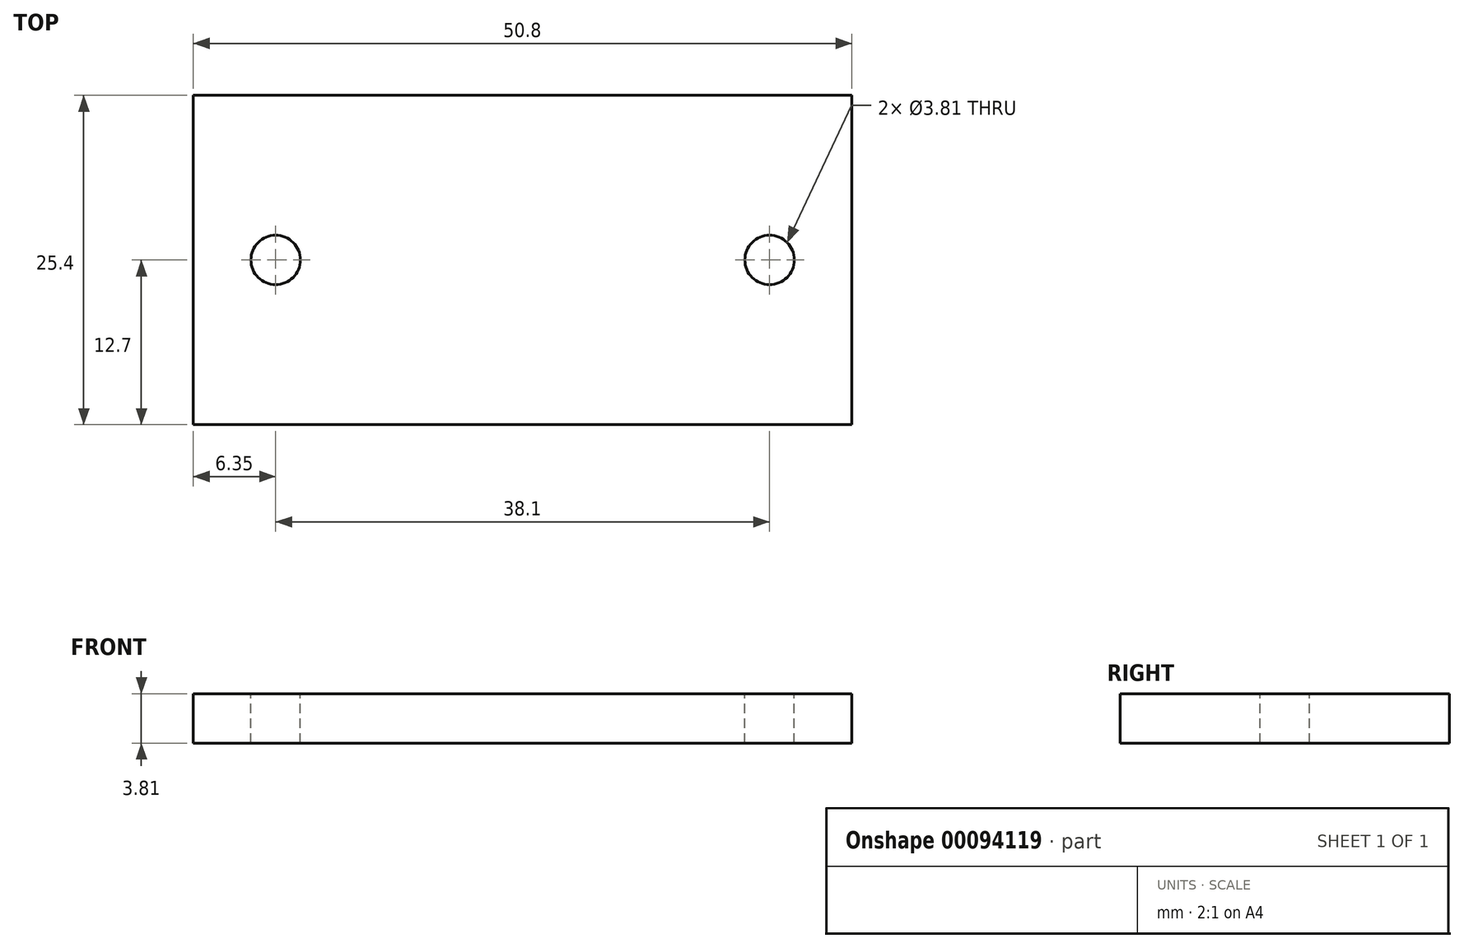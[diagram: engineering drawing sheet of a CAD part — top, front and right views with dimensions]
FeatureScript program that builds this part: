
annotation { "Feature Type Name" : "Feature", "Feature Type Description" : "" }
export const myFeature = defineFeature(function(context is Context, id is Id, definition is map)
    precondition{}
    {
        {
            var Q0;
            Q0=qCreatedBy(makeId("Front.planeOp"),FACE);
            var sketch = newSketch(context, id + "F0", { "sketchPlane" : qUnion([Q0])});
            skLineSegment(sketch, "E0.bottom", {"start": v(-25.4, 0) * mm, "end": v(25.4, 0) * mm});
            skLineSegment(sketch, "E0.top", {"start": v(-25.4, 3.81) * mm, "end": v(25.4, 3.8) * mm});
            skLineSegment(sketch, "E0.left", {"start": v(-25.4, 0) * mm, "end": v(-25.4, 3.81) * mm});
            skLineSegment(sketch, "E0.right", {"start": v(25.4, 0) * mm, "end": v(25.4, 3.81) * mm});
            skLineSegment(sketch, "E1.bottom", {"start": v(-12.7, 3.81) * mm, "end": v(12.7, 3.8) * mm});
            skLineSegment(sketch, "E1.top", {"start": v(-12.7, 29.21) * mm, "end": v(12.7, 29.21) * mm});
            skLineSegment(sketch, "E1.left", {"start": v(-12.7, 3.8) * mm, "end": v(-12.7, 29.21) * mm});
            skLineSegment(sketch, "E1.right", {"start": v(12.7, 3.8) * mm, "end": v(12.7, 29.21) * mm});
            skPoint(sketch, "E2", {"position": v(0, 3.8) * mm});
            skSolve(sketch);
        }
        {
            var Q0;
            Q0=makeQuery(id+"F0.imprint","IMPRINT",FACE,{"disambiguationData":[TD([[makeQuery(id+"F0.imprint","IMPRINT",EDGE,{"derivedFrom":sQuery(id+"F0.wireOp",EDGE,"E1.bottom")}),1.0]])]});
            var Q1;
            Q1=makeQuery(id+"F0.imprint","IMPRINT",FACE,{"disambiguationData":[TD([[makeQuery(id+"F0.imprint","IMPRINT",EDGE,{"derivedFrom":sQuery(id+"F0.wireOp",EDGE,"E0.bottom")}),1.0]])]});
            extrude(context, id + "F1", {"entities" : qUnion([Q0, Q1]), "depth" : 25.4 * mm});
        }
        {
            var Q0;
            Q0=makeQuery(id+"F1.opExtrude","CAP_FACE",FACE,{"disambiguationData":[OSD([sQuery(id+"F0.wireOp",EDGE,"E0.bottom"),sQuery(id+"F0.wireOp",EDGE,"E0.top"),sQuery(id+"F0.wireOp",EDGE,"E0.left"),sQuery(id+"F0.wireOp",EDGE,"E0.right"),sQuery(id+"F0.wireOp",EDGE,"E1.top"),sQuery(id+"F0.wireOp",EDGE,"E1.left"),sQuery(id+"F0.wireOp",EDGE,"E1.right")])],"isStart":true});
            var sketch = newSketch(context, id + "F2", { "sketchPlane" : qUnion([Q0])});
            skCircle(sketch, "E3", {"center": v(0, 16.51) * mm, "radius": 4 * mm});
            skSolve(sketch);
        }
        {
            var Q0;
            Q0=makeQuery(id+"F2.imprint","IMPRINT",FACE,{"disambiguationData":[TD([[makeQuery(id+"F2.imprint","IMPRINT",EDGE,{"derivedFrom":sQuery(id+"F2.wireOp",EDGE,"E3")}),1.0]])]});
            extrude(context, id + "F3", {"entities" : qUnion([Q0]), "operationType" : NewBodyOperationType.REMOVE, "endBound" : BoundingType.THROUGH_ALL, "oppositeDirection" : true, "depth" : 25.4 * mm});
        }
        {
            var Q0;
            Q0=makeQuery(id+"F1.opExtrude","CAP_FACE",FACE,{"disambiguationData":[OSD([sQuery(id+"F0.wireOp",EDGE,"E0.bottom"),sQuery(id+"F0.wireOp",EDGE,"E0.top"),sQuery(id+"F0.wireOp",EDGE,"E0.left"),sQuery(id+"F0.wireOp",EDGE,"E0.right"),sQuery(id+"F0.wireOp",EDGE,"E1.top"),sQuery(id+"F0.wireOp",EDGE,"E1.left"),sQuery(id+"F0.wireOp",EDGE,"E1.right")])],"isStart":true});
            var sketch = newSketch(context, id + "F4", { "sketchPlane" : qUnion([Q0])});
            skCircle(sketch, "E4.0", {"center": v(0, 16.51) * mm, "radius": 4 * mm});
            skCircle(sketch, "E5.cCircle", {"center": v(0, 16.51) * mm, "radius": 6.35 * mm, "construction": true});
            skLineSegment(sketch, "E5.0", {"start": v(3.67, 22.86) * mm, "end": v(7.33, 16.51) * mm});
            skLineSegment(sketch, "E5.1", {"start": v(7.33, 16.51) * mm, "end": v(3.67, 10.16) * mm});
            skLineSegment(sketch, "E5.2", {"start": v(3.67, 10.16) * mm, "end": v(-3.67, 10.16) * mm});
            skLineSegment(sketch, "E5.3", {"start": v(-3.67, 10.16) * mm, "end": v(-7.33, 16.5) * mm});
            skLineSegment(sketch, "E5.4", {"start": v(-7.33, 16.51) * mm, "end": v(-3.67, 22.86) * mm});
            skLineSegment(sketch, "E5.5", {"start": v(-3.67, 22.86) * mm, "end": v(3.67, 22.86) * mm});
            skPoint(sketch, "E5.0.midPoint", {"position": v(5.5, 19.69) * mm});
            skSolve(sketch);
        }
        {
            var Q0;
            Q0=makeQuery(id+"F4.imprint","IMPRINT",FACE,{"disambiguationData":[TD([[makeQuery(id+"F4.imprint","IMPRINT",EDGE,{"derivedFrom":sQuery(id+"F4.wireOp",EDGE,"E4.0")}),-1.0]])]});
            extrude(context, id + "F5", {"entities" : qUnion([Q0]), "operationType" : NewBodyOperationType.REMOVE, "oppositeDirection" : true, "depth" : 7.62 * mm});
        }
        {
            var Q0;
            {var subQ0=sQuery(id+"F0.wireOp",EDGE,"E0.top");Q0=makeQuery(id+"F1.opExtrude","SWEPT_FACE",FACE,{"disambiguationData":[OSD([subQ0]),TDD([makeQuery(id+"F0.imprint","IMPRINT",EDGE,{"disambiguationData":[TD([[makeQuery(id+"F0.imprint","INTERSECT",VERTEX,{"derivedFrom":[subQ0,sQuery(id+"F0.wireOp",EDGE,"E0.right")]}),1.0]])],"derivedFrom":subQ0})])]});}
            var sketch = newSketch(context, id + "F6", { "sketchPlane" : qUnion([Q0])});
            skLineSegment(sketch, "E6.0.0", {"start": v(-25.4, 0) * mm, "end": v(25.4, 0) * mm});
            skLineSegment(sketch, "E6.0.1", {"start": v(25.4, 0) * mm, "end": v(25.4, -25.4) * mm});
            skLineSegment(sketch, "E6.0.2", {"start": v(25.4, -25.4) * mm, "end": v(-25.4, -25.4) * mm});
            skLineSegment(sketch, "E6.0.3", {"start": v(-25.4, -25.4) * mm, "end": v(-25.4, 0) * mm});
            skLineSegment(sketch, "E7.0", {"start": v(12.7, -25.4) * mm, "end": v(12.7, 0) * mm});
            skLineSegment(sketch, "E8", {"start": v(19.05, 0) * mm, "end": v(19.05, -25.4) * mm, "construction": true});
            skLineSegment(sketch, "E9.0", {"start": v(-12.7, -25.4) * mm, "end": v(-12.7, 0) * mm});
            skLineSegment(sketch, "E10.0.0", {"start": v(-12.7, 0) * mm, "end": v(-25.4, 0) * mm});
            skLineSegment(sketch, "E10.0.1", {"start": v(-25.4, 0) * mm, "end": v(-25.4, -25.4) * mm});
            skLineSegment(sketch, "E10.0.2", {"start": v(-25.4, -25.4) * mm, "end": v(-12.7, -25.4) * mm});
            skLineSegment(sketch, "E11", {"start": v(-19.05, 0) * mm, "end": v(-19.05, -25.4) * mm, "construction": true});
            skCircle(sketch, "E12", {"center": v(-19.05, -12.7) * mm, "radius": 1.9 * mm});
            skCircle(sketch, "E13", {"center": v(19.05, -12.7) * mm, "radius": 1.9 * mm});
            skSolve(sketch);
        }
        {
            var Q0;
            Q0=makeQuery(id+"F6.imprint","IMPRINT",FACE,{"disambiguationData":[TD([[makeQuery(id+"F6.imprint","IMPRINT",EDGE,{"derivedFrom":sQuery(id+"F6.wireOp",EDGE,"E12")}),1.0]])]});
            var Q1;
            Q1=makeQuery(id+"F6.imprint","IMPRINT",FACE,{"disambiguationData":[TD([[makeQuery(id+"F6.imprint","IMPRINT",EDGE,{"derivedFrom":sQuery(id+"F6.wireOp",EDGE,"E13")}),1.0]])]});
            extrude(context, id + "F7", {"entities" : qUnion([Q0, Q1]), "operationType" : NewBodyOperationType.REMOVE, "oppositeDirection" : true, "depth" : 25.4 * mm});
        }
    });
